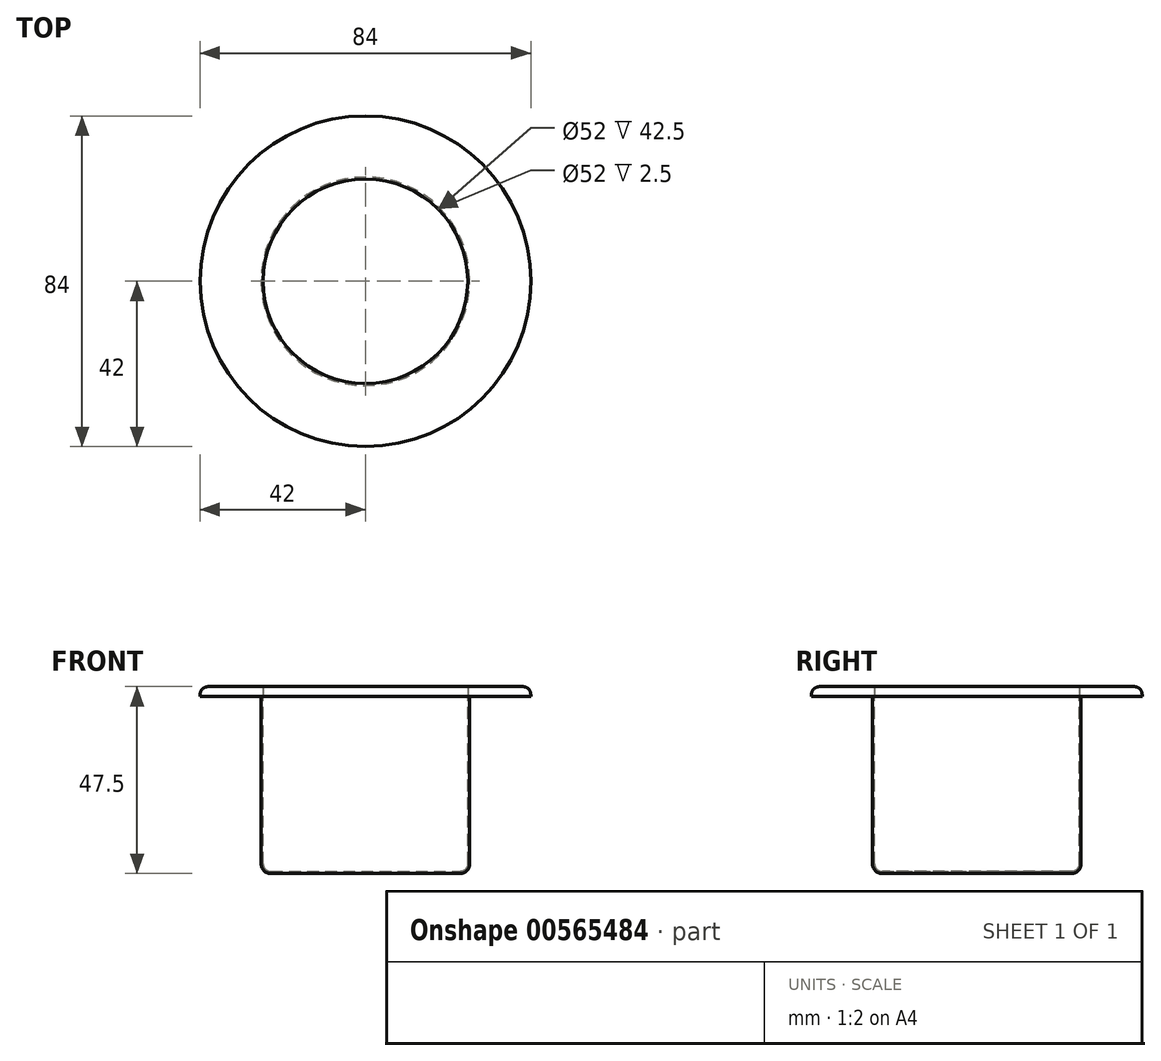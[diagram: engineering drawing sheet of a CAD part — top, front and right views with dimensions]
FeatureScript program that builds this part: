
annotation { "Feature Type Name" : "Feature", "Feature Type Description" : "" }
export const myFeature = defineFeature(function(context is Context, id is Id, definition is map)
    precondition{}
    {
        {
            var Q0;
            Q0=qCreatedBy(makeId("Top.planeOp"),FACE);
            var sketch = newSketch(context, id + "F0", { "sketchPlane" : qUnion([Q0])});
            skCircle(sketch, "E0", {"center": v(0, 0) * mm, "radius": 42 * mm});
            skCircle(sketch, "E1", {"center": v(0, 0) * mm, "radius": 26 * mm});
            skSolve(sketch);
        }
        {
            var Q0;
            Q0=makeQuery(id+"F0.imprint","IMPRINT",FACE,{"disambiguationData":[TD([[makeQuery(id+"F0.imprint","IMPRINT",EDGE,{"derivedFrom":sQuery(id+"F0.wireOp",EDGE,"E0")}),1.0]])]});
            extrude(context, id + "F1", {"entities" : qUnion([Q0]), "depth" : 2.5 * mm, "offsetDistance" : 25 * mm});
        }
        {
            var Q0;
            Q0=makeQuery(id+"F1.opExtrude","CAP_EDGE",EDGE,{"disambiguationData":[OSD([sQuery(id+"F0.wireOp",EDGE,"E0")])],"isStart":false});
            fillet(context, id + "F2", {"entities" : qUnion([Q0]), "radius" : 2 * mm, "tangentPropagation" : true, "allowEdgeOverflow" : false});
        }
        {
            var Q0;
            Q0=makeQuery(id+"F1.opExtrude","CAP_FACE",FACE,{"disambiguationData":[OSD([sQuery(id+"F0.wireOp",EDGE,"E0"),sQuery(id+"F0.wireOp",EDGE,"E1")])],"isStart":true});
            var sketch = newSketch(context, id + "F3", { "sketchPlane" : qUnion([Q0])});
            skCircle(sketch, "E2", {"center": v(0, 0) * mm, "radius": 26.5 * mm});
            skSolve(sketch);
        }
        {
            var Q0;
            Q0 = qSketchRegion(id + "F3", true);
            extrude(context, id + "F4", {"entities" : qUnion([Q0]), "depth" : 45 * mm, "offsetDistance" : 25 * mm});
        }
        {
            var Q0;
            Q0=makeQuery(id+"F4.opExtrude","CAP_EDGE",EDGE,{"disambiguationData":[OSD([sQuery(id+"F3.wireOp",EDGE,"E2")])],"isStart":false});
            fillet(context, id + "F5", {"entities" : qUnion([Q0]), "radius" : 2.5 * mm, "tangentPropagation" : true, "allowEdgeOverflow" : false});
        }
        {
            var Q0;
            Q0=makeQuery(id+"F4.opExtrude","CAP_FACE",FACE,{"disambiguationData":[OSD([sQuery(id+"F3.wireOp",EDGE,"E2")])],"isStart":true});
            shell(context, id + "F6", {"entities" : qUnion([Q0]), "thickness" : .5 * mm});
        }
    });
